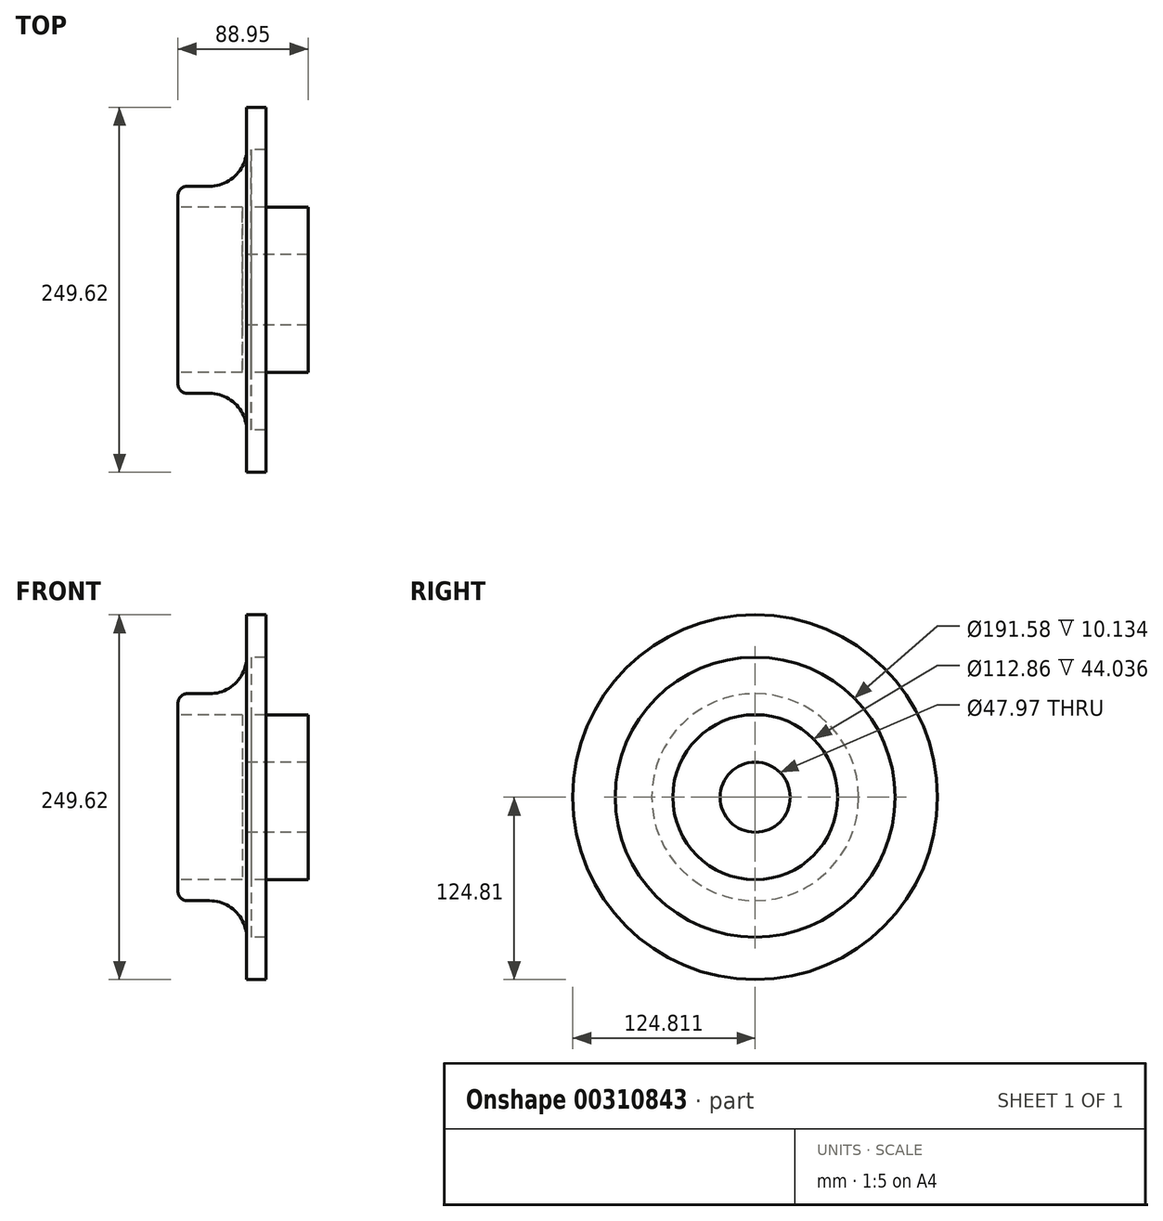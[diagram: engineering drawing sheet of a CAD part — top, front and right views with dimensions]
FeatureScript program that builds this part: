
annotation { "Feature Type Name" : "Feature", "Feature Type Description" : "" }
export const myFeature = defineFeature(function(context is Context, id is Id, definition is map)
    precondition{}
    {
        {
            var Q0;
            Q0=qCreatedBy(makeId("Top.planeOp"),FACE);
            var sketch = newSketch(context, id + "F0", { "sketchPlane" : qUnion([Q0])});
            skLineSegment(sketch, "E0.bottom", {"start": v(-44.91, -32.44) * mm, "end": v(0, -32.44) * mm});
            skLineSegment(sketch, "E0.top", {"start": v(-44.91, 0) * mm, "end": v(0, 0) * mm});
            skLineSegment(sketch, "E0.left", {"start": v(-44.91, -32.44) * mm, "end": v(-44.91, 0) * mm});
            skLineSegment(sketch, "E0.right", {"start": v(0, -32.44) * mm, "end": v(0, 0) * mm});
            skLineSegment(sketch, "E1.bottom", {"start": v(-44.91, 0) * mm, "end": v(-38.86, 0) * mm});
            skLineSegment(sketch, "E1.top", {"start": v(-42, 68.38) * mm, "end": v(-38.86, 68.38) * mm});
            skLineSegment(sketch, "E1.left", {"start": v(-42, 39.8) * mm, "end": v(-42, 68.38) * mm});
            skLineSegment(sketch, "E1.right", {"start": v(-38.86, 0) * mm, "end": v(-38.86, 68.38) * mm});
            skLineSegment(sketch, "E2.bottom", {"start": v(-38.86, 68.38) * mm, "end": v(-28.73, 68.38) * mm});
            skLineSegment(sketch, "E2.top", {"start": v(-38.86, 39.36) * mm, "end": v(-28.73, 39.36) * mm});
            skLineSegment(sketch, "E2.left", {"start": v(-38.86, 68.38) * mm, "end": v(-38.86, 39.36) * mm});
            skLineSegment(sketch, "E2.right", {"start": v(-28.73, 68.38) * mm, "end": v(-28.73, 39.36) * mm});
            skLineSegment(sketch, "E3.bottom", {"start": v(-44.91, 0) * mm, "end": v(-88.95, 0) * mm});
            skLineSegment(sketch, "E3.top", {"start": v(-67.4, 14.4) * mm, "end": v(-82.6, 14.4) * mm});
            skLineSegment(sketch, "E3.left", {"start": v(-44.91, 0) * mm, "end": v(-44.91, 6.56) * mm});
            skLineSegment(sketch, "E3.right", {"start": v(-88.95, 0) * mm, "end": v(-88.95, 8.06) * mm});
            skArc(sketch, "E4.filletArc", {"start": v(-67.4, 14.4) * mm, "mid": v(-49.44, 21.85) * mm, "end": v(-42, 39.8) * mm});
            skPoint(sketch, "E5.visualSharp", {"position": v(-88.95, 14.4) * mm});
            skArc(sketch, "E5.filletArc", {"start": v(-82.6, 14.4) * mm, "mid": v(-87.09, 12.55) * mm, "end": v(-88.95, 8.06) * mm});
            skSolve(sketch);
        }
        {
            var Q0;
            Q0=qCreatedBy(makeId("Top.planeOp"),FACE);
            var sketch = newSketch(context, id + "F1", { "sketchPlane" : qUnion([Q0])});
            skLineSegment(sketch, "E6", {"start": v(-55.7, -56.43) * mm, "end": v(38.26, -56.43) * mm});
            skSolve(sketch);
        }
        {
            var Q0;
            Q0 = qSketchRegion(id + "F0", true);
            var Q1;
            Q1=sQuery(id+"F1.wireOp",EDGE,"E6");
            revolve(context, id + "F2", {"entities" : qUnion([Q0]), "axis" : qUnion([Q1]), "revolveType" : RevolveType.FULL});
        }
    });
